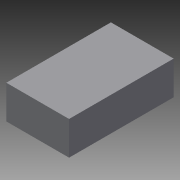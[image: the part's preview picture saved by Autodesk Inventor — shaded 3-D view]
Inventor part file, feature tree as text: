
AUTODESK INVENTOR PART (.ipt)
format: ipt  version: 2015 (Build 190159000, 159)  size: 68,608 bytes
history: native  units: in
note: dims shown in document units (in); Inventor stores cm internally (conversion verified against a paired STEP export)
features: extrude x1, sketch x1
ambient origin geometry x8: Origin, YZ Plane, XZ Plane, XY Plane, X Axis, Y Axis, Z Axis, Center Point
bodies: Solid1 (feature_tree)
feature tree (2):
  extrude  "Extrusion1"  Depth=2.4016in
  sketch  "Sketch1"  dims[d0=4.5in d1=2.4016in d2=7.5in d3=0.0in]
